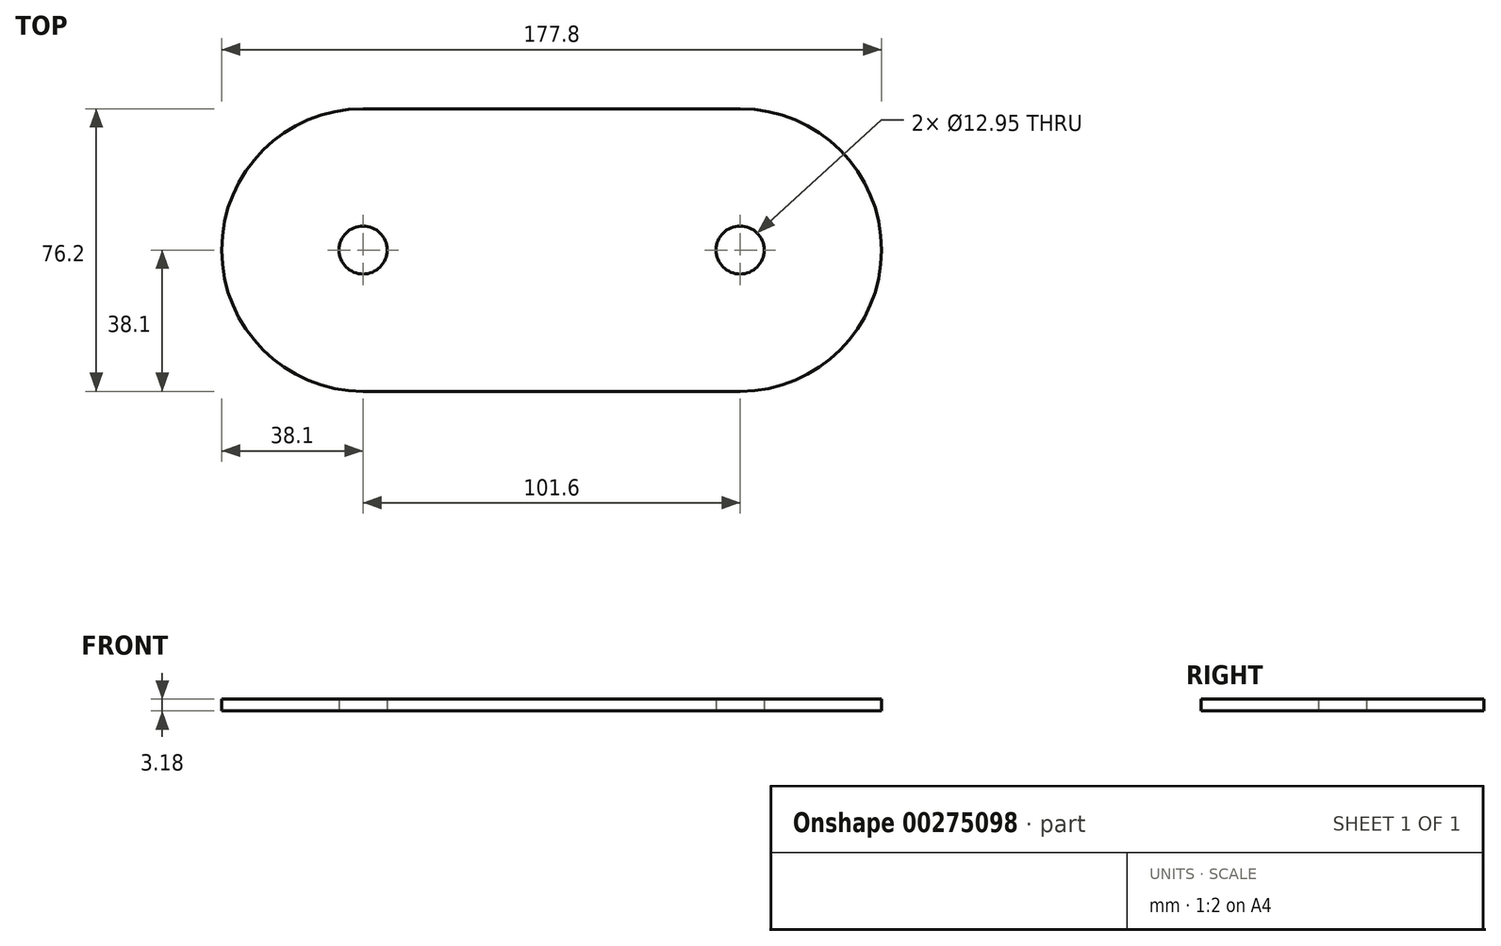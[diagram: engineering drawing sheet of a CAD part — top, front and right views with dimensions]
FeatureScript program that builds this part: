
annotation { "Feature Type Name" : "Feature", "Feature Type Description" : "" }
export const myFeature = defineFeature(function(context is Context, id is Id, definition is map)
    precondition{}
    {
        {
            var Q0;
            Q0=qCreatedBy(makeId("Top.planeOp"),FACE);
            var sketch = newSketch(context, id + "F0", { "sketchPlane" : qUnion([Q0])});
            skLineSegment(sketch, "E0.bottom", {"start": v(-38.1, 38.1) * mm, "end": v(63.5, 38.1) * mm});
            skLineSegment(sketch, "E0.top", {"start": v(-38.1, -38.1) * mm, "end": v(63.5, -38.1) * mm});
            skLineSegment(sketch, "E0.left", {"start": v(-38.1, 38.1) * mm, "end": v(-38.1, -38.1) * mm});
            skLineSegment(sketch, "E0.right", {"start": v(63.5, 38.1) * mm, "end": v(63.5, -38.1) * mm});
            skArc(sketch, "E1", {"start": v(-38.1, 38.1) * mm, "mid": v(-76.2, 0) * mm, "end": v(-38.1, -38.1) * mm});
            skArc(sketch, "E2", {"start": v(63.5, -38.1) * mm, "mid": v(101.6, 0) * mm, "end": v(63.5, 38.1) * mm});
            skCircle(sketch, "E3", {"center": v(63.5, 0) * mm, "radius": 6.48 * mm});
            skCircle(sketch, "E4", {"center": v(-38.1, 0) * mm, "radius": 6.48 * mm});
            skSolve(sketch);
        }
        {
            var Q0;
            Q0=qSketchRegion(id+"F0",true);
            extrude(context, id + "F1", {"entities" : qUnion([Q0]), "depth" : 3.17 * mm});
        }
    });
